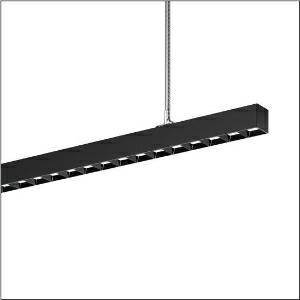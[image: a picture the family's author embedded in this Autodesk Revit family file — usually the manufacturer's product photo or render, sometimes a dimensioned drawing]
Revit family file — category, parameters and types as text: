
# Revit family: silica_r__21_51mx32dc3dbb_53cb
name_source: partatom
category: Lighting Fixtures
units: mm (PartAtom-declared; Revit-internal decimal feet)

## family parameters
Cut with Voids When Loaded = No
Host = Face
Light Source = No
Part Type = Normal
Room Calculation Point = No
Round Connector Dimension = Use Diameter
Shared = No

## types (1)
- --- (1 x LED, 18220 lm, 113 W, 3000K)
    Apparent Load = 113 VA
    CIE Flux Codes = 86 99 100 59 100
    Color Rendering = 80
    Color Temperature = 3000K
    Default Elevation = 1800 mm
    Description = Silica® 21, office luminaire, primary light control with darklight reflector, of PMMA, black, CAT 2 (L<= 3000cd/m²), light emission: direct/indirect distribution, primary light characteristic: symmetric, installation type: suspended mounting, LED, rated luminous flux: 18.220lm, luminous efficacy: 161lm/W, light colour: 830, colour temperature: 3000K, with terminal, 3+2-pole, max. 2.5mm², mains connection: 220..240V, AC, 50/60Hz, rated input power: 113W, luminaire housing, of aluminium, jet black (RAL 9005), length: 3.004mm, width: 53mm, height: 53mm, protection rating (complete): IP20, insulation class (complete): insulation class I (protective earthing), certification: CE, permissible operating ambient temperature: 0..+35°C, standard: EN 50419, packaging unit: 1 piece
    Height = 53 mm
    Lamp = 1 x LED
    Lamp Light Flux = 18220 lm
    Lamp Power = 113 W
    Lamp count = 1
    Length = 3004 mm
    Luminous efficacy = 161 lm/W
    Manufacturer = Siteco
    ModVariant = No
    Model = 51MX32DC3DBB
    Mounting Place = Ceiling
    Mounting Type = Pendant
    Number of Poles = 1
    OnlyDefault = Yes
    Power Factor = 1
    Product Name = Silica® 21
    Product group = office luminaire | ceiling pendant
    ProductGroupID = 905
    Protection Class = Protection class I
    Protection Degree = IP 20
    RLX_Detail_Level = 1
    RlxData = <blob elided: 66581 chars, md5=7c40cd62>
    Socket = socket
    Standby Power = 0 W
    System Light Flux = 18220 lm
    System Power = 113 W
    Type Comments = factory setting: luminous flux: 100 % | dim-lin: 254 | 391 mA
    Type Image = l_1251718.jpg
    URL = http://relux.com
    VarID = @adj_031253
    Voltage = 0 V
    Weight = 0.00 kg
    Width = 53 mm

## geometry (parser evidence)
native form markers: Blend x4, Sweep x12
no freeform markers — native parametric forms only
